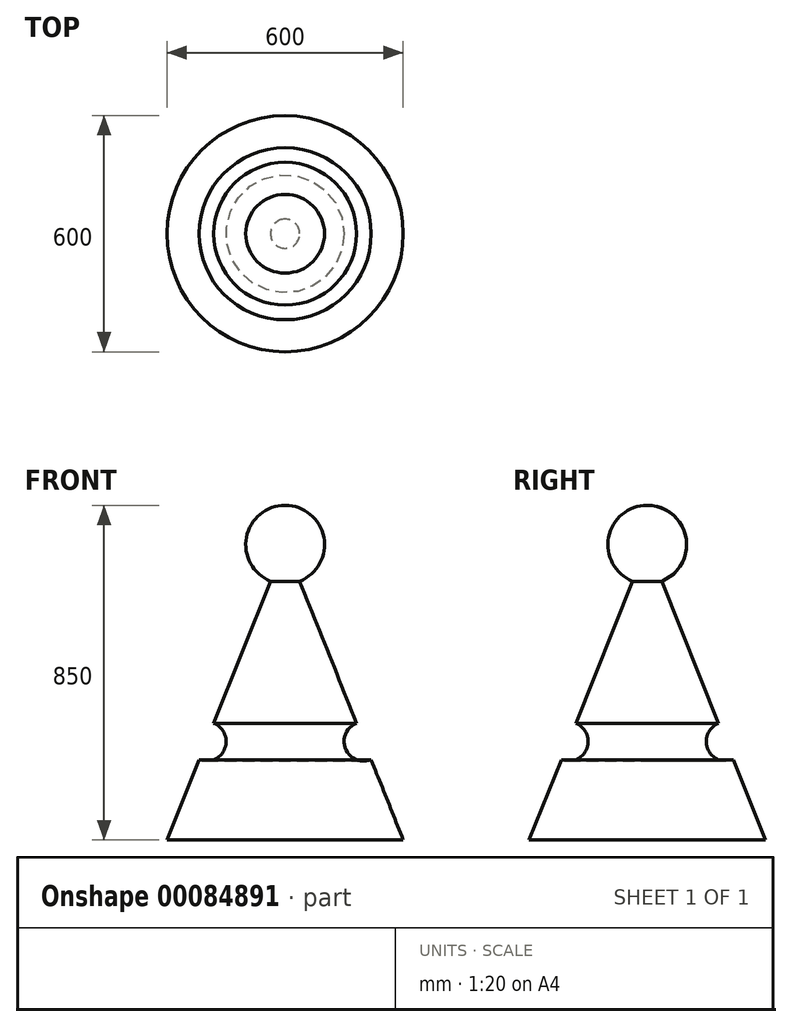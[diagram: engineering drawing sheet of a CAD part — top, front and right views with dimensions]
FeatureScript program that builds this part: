
annotation { "Feature Type Name" : "Feature", "Feature Type Description" : "" }
export const myFeature = defineFeature(function(context is Context, id is Id, definition is map)
    precondition{}
    {
        {
            var Q0;
            Q0=qCreatedBy(makeId("Right.planeOp"),FACE);
            var sketch = newSketch(context, id + "F0", { "sketchPlane" : qUnion([Q0])});
            skLineSegment(sketch, "E0", {"start": v(0, 886.19) * mm, "end": v(0, -75.4) * mm, "construction": true});
            skArc(sketch, "E1", {"start": v(0, 774.6) * mm, "mid": v(-98.2, 693.51) * mm, "end": v(-37.14, 581.75) * mm});
            skLineSegment(sketch, "E2", {"start": v(0, -75.4) * mm, "end": v(-300, -75.4) * mm});
            skLineSegment(sketch, "E3", {"start": v(-300, -75.4) * mm, "end": v(-218.57, 128.18) * mm});
            skArc(sketch, "E4", {"start": v(-218.57, 128.18) * mm, "mid": v(-153.58, 156.03) * mm, "end": v(-181.43, 221.03) * mm});
            skLineSegment(sketch, "E5", {"start": v(0, 774.6) * mm, "end": v(0, -75.4) * mm});
            skLineSegment(sketch, "E6.trimOffspring", {"start": v(-181.43, 221.03) * mm, "end": v(-37.14, 581.75) * mm});
            skSolve(sketch);
        }
        {
            var Q0;
            Q0 = qSketchRegion(id + "F0", true);
            var Q1;
            Q1=sQuery(id+"F0.wireOp",EDGE,"E5");
            revolve(context, id + "F1", {"entities" : qUnion([Q0]), "axis" : qUnion([Q1]), "revolveType" : RevolveType.FULL});
        }
    });
